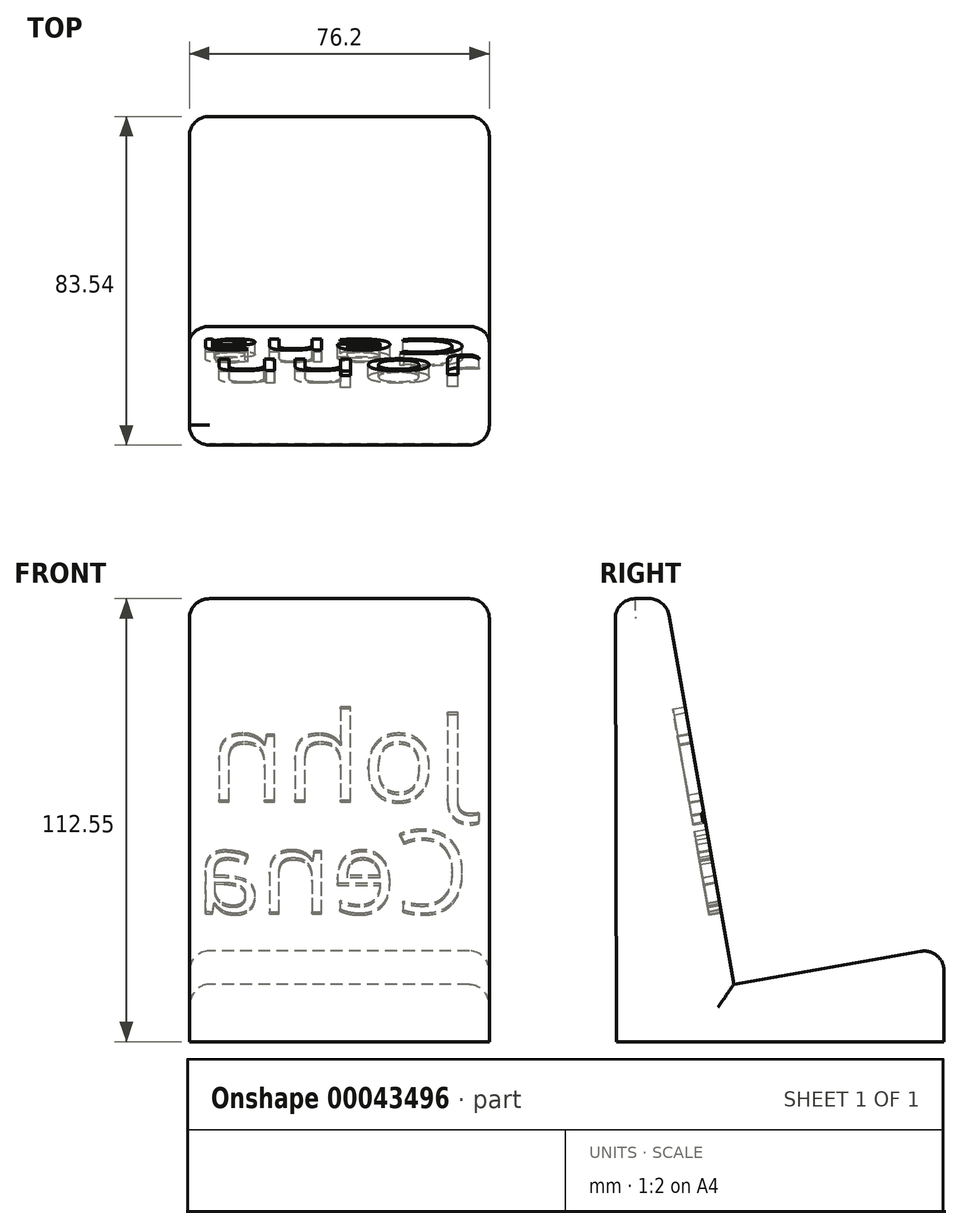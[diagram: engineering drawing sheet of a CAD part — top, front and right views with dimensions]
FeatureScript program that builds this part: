
annotation { "Feature Type Name" : "Feature", "Feature Type Description" : "" }
export const myFeature = defineFeature(function(context is Context, id is Id, definition is map)
    precondition{}
    {
        {
            var Q0;
            Q0=qCreatedBy(makeId("Right.planeOp"),FACE);
            var sketch = newSketch(context, id + "F0", { "sketchPlane" : qUnion([Q0])});
            skLineSegment(sketch, "E0", {"start": v(50.8, 0) * mm, "end": v(0, 0) * mm});
            skLineSegment(sketch, "E1", {"start": v(-32.76, 112.53) * mm, "end": v(-19.85, 112.56) * mm});
            skLineSegment(sketch, "E2", {"start": v(-2.57, 14.6) * mm, "end": v(50.8, 24) * mm});
            skLineSegment(sketch, "E3", {"start": v(50.8, 24) * mm, "end": v(50.8, 0) * mm});
            skLineSegment(sketch, "E4", {"start": v(-32.76, 112.53) * mm, "end": v(-32.43, 0) * mm});
            skLineSegment(sketch, "E5", {"start": v(-32.43, 0) * mm, "end": v(0, 0) * mm});
            skLineSegment(sketch, "E6", {"start": v(-19.85, 112.56) * mm, "end": v(-2.57, 14.6) * mm});
            skSolve(sketch);
        }
        {
            var Q0;
            Q0=makeQuery(id+"F0.imprint","IMPRINT",FACE,{"disambiguationData":[TD([[makeQuery(id+"F0.imprint","IMPRINT",EDGE,{"derivedFrom":sQuery(id+"F0.wireOp",EDGE,"E0")}),-1.0]])]});
            extrude(context, id + "F1", {"entities" : qUnion([Q0]), "depth" : 76.2 * mm});
        }
        {
            var Q0;
            Q0=makeQuery(id+"F1.opExtrude","CAP_EDGE",EDGE,{"disambiguationData":[OSD([sQuery(id+"F0.wireOp",EDGE,"E1")])],"isStart":false});
            fillet(context, id + "F2", {"entities" : qUnion([Q0]), "radius" : 5.08 * mm, "tangentPropagation" : true, "allowEdgeOverflow" : false});
        }
        {
            var Q0;
            Q0=makeQuery(id+"F1.opExtrude","SWEPT_EDGE",EDGE,{"disambiguationData":[OSD([sQuery(id+"F0.wireOp",EDGE,"E1"),sQuery(id+"F0.wireOp",EDGE,"E6")])]});
            fillet(context, id + "F3", {"entities" : qUnion([Q0]), "radius" : 5.08 * mm, "tangentPropagation" : true, "allowEdgeOverflow" : false});
        }
        {
            var Q0;
            Q0=makeQuery(id+"F1.opExtrude","CAP_EDGE",EDGE,{"disambiguationData":[OSD([sQuery(id+"F0.wireOp",EDGE,"E4")])],"isStart":false});
            var Q1;
            Q1=makeQuery(id+"F1.opExtrude","CAP_EDGE",EDGE,{"disambiguationData":[OSD([sQuery(id+"F0.wireOp",EDGE,"E6")])],"isStart":true});
            fillet(context, id + "F4", {"entities" : qUnion([Q0, Q1]), "radius" : 5.08 * mm, "tangentPropagation" : true, "allowEdgeOverflow" : false});
        }
        {
            var Q0;
            Q0=makeQuery(id+"F1.opExtrude","CAP_EDGE",EDGE,{"disambiguationData":[OSD([sQuery(id+"F0.wireOp",EDGE,"E2")])],"isStart":false});
            fillet(context, id + "F5", {"entities" : qUnion([Q0]), "radius" : 5.08 * mm, "tangentPropagation" : true, "allowEdgeOverflow" : false});
        }
        {
            var Q0;
            Q0=makeQuery(id+"F1.opExtrude","SWEPT_EDGE",EDGE,{"disambiguationData":[OSD([sQuery(id+"F0.wireOp",EDGE,"E2"),sQuery(id+"F0.wireOp",EDGE,"E3")])]});
            fillet(context, id + "F6", {"entities" : qUnion([Q0]), "radius" : 5.08 * mm, "tangentPropagation" : true, "allowEdgeOverflow" : false});
        }
        {
            var Q0;
            Q0=makeQuery(id+"F1.opExtrude","CAP_EDGE",EDGE,{"disambiguationData":[OSD([sQuery(id+"F0.wireOp",EDGE,"E4")])],"isStart":true});
            fillet(context, id + "F7", {"entities" : qUnion([Q0]), "radius" : 5.08 * mm, "tangentPropagation" : true, "allowEdgeOverflow" : false});
        }
        {
            var Q0;
            Q0=makeQuery(id+"F1.opExtrude","CAP_EDGE",EDGE,{"disambiguationData":[OSD([sQuery(id+"F0.wireOp",EDGE,"E2")])],"isStart":true});
            fillet(context, id + "F8", {"entities" : qUnion([Q0]), "radius" : 5.08 * mm, "tangentPropagation" : true, "allowEdgeOverflow" : false});
        }
        {
            var Q0;
            Q0=makeQuery(id+"F1.opExtrude","SWEPT_FACE",FACE,{"disambiguationData":[OSD([sQuery(id+"F0.wireOp",EDGE,"E6")])]});
            var sketch = newSketch(context, id + "F9", { "sketchPlane" : qUnion([Q0])});
            skText(sketch, "E7", { "text": "John", "fontName": "OpenSans-Regular.ttf"});
            skText(sketch, "E8", { "text": "Cena", "fontName": "OpenSans-Regular.ttf"});
            const initialGuessF9  = {"E7": [-0.07112, 0.06242, 1, 0, 0.02268], "E8": [-0.07112, 0.0335, 1, 0, 0.02116]};
            skSetInitialGuess(sketch, initialGuessF9);
            skSolve(sketch);
        }
        {
            var Q0;
            Q0 = qSketchRegion(id + "F9", true);
            extrude(context, id + "F10", {"entities" : qUnion([Q0]), "operationType" : NewBodyOperationType.REMOVE, "oppositeDirection" : true, "depth" : 3.17 * mm});
        }
    });
